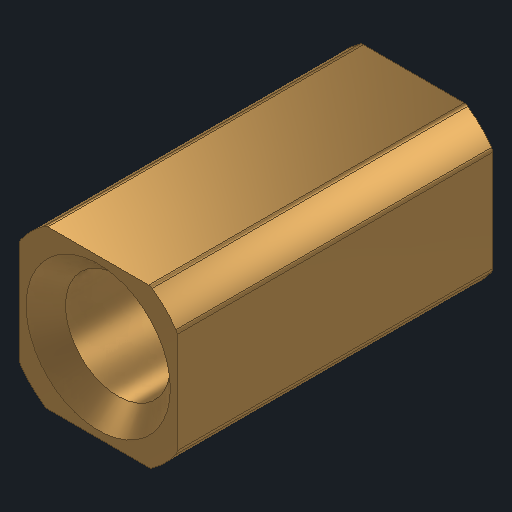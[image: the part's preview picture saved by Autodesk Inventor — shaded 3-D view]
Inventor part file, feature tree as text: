
AUTODESK INVENTOR PART (.ipt)
format: ipt  version: 2025 (Build 290162000, 162)  size: 162,816 bytes
history: native  units: in
note: dims shown in document units (in); Inventor stores cm internally (conversion verified against a paired STEP export)
features: other x3, sketch x2
ambient origin geometry x8: Origin, YZ Plane, XZ Plane, XY Plane, X Axis, Y Axis, Z Axis, Center Point
bodies: Solid1 (feature_tree)
feature tree (5):
  other  "HS Shaft Adapter Circle.ipt"
  other  "Solid1::HS Shaft Adapter Circle.ipt"
  other  "TaggingFeature1"
  sketch  "Sketch1"  dims[d0=0.3937in]
  sketch  "Sketch2"
